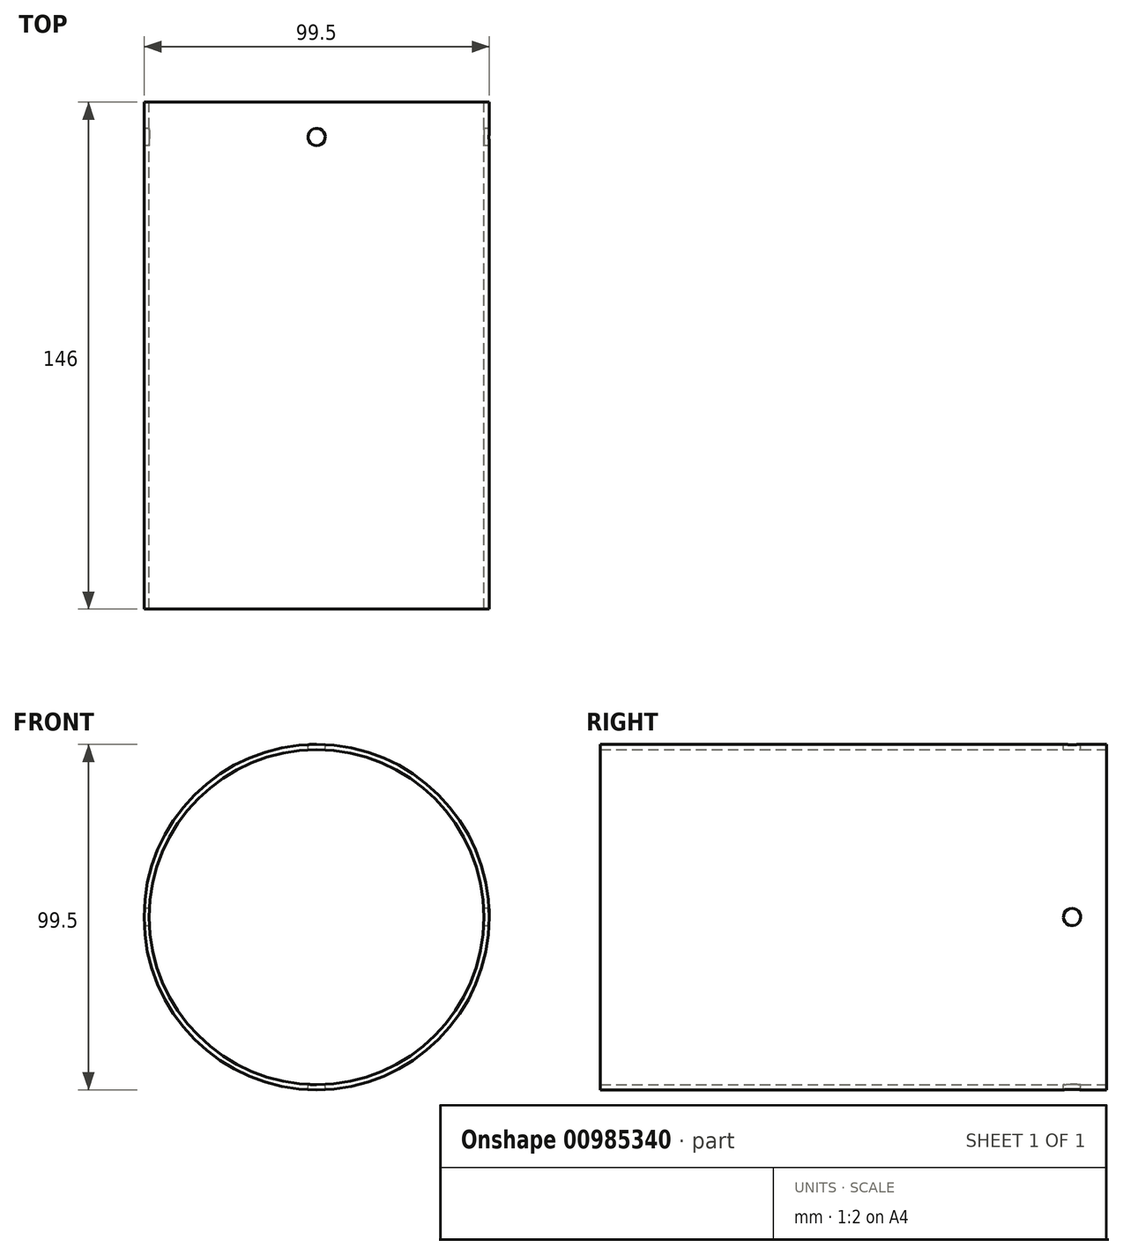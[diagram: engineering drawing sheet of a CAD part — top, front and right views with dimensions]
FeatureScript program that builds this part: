
annotation { "Feature Type Name" : "Feature", "Feature Type Description" : "" }
export const myFeature = defineFeature(function(context is Context, id is Id, definition is map)
    precondition{}
    {
        {
            var Q0;
            Q0=qCreatedBy(makeId("Front.planeOp"),FACE);
            var sketch = newSketch(context, id + "F0", { "sketchPlane" : qUnion([Q0])});
            skCircle(sketch, "E0", {"center": v(0, 0) * mm, "radius": 48.25 * mm});
            skCircle(sketch, "E1", {"center": v(0, 0) * mm, "radius": 49.75 * mm});
            skSolve(sketch);
        }
        {
            var Q0;
            Q0=makeQuery(id+"F0.imprint","IMPRINT",FACE,{"disambiguationData":[TD([[makeQuery(id+"F0.imprint","IMPRINT",EDGE,{"derivedFrom":sQuery(id+"F0.wireOp",EDGE,"E0")}),-1.0]])]});
            extrude(context, id + "F1", {"entities" : qUnion([Q0]), "endBound" : BoundingType.SYMMETRIC, "depth" : 146 * mm});
        }
        {
            var Q0;
            Q0=qCreatedBy(makeId("Top.planeOp"),FACE);
            var sketch = newSketch(context, id + "F2", { "sketchPlane" : qUnion([Q0])});
            skCircle(sketch, "E2", {"center": v(0, 63) * mm, "radius": 2.5 * mm});
            skSolve(sketch);
        }
        {
            var Q0;
            Q0=qCreatedBy(makeId("Right.planeOp"),FACE);
            var sketch = newSketch(context, id + "F3", { "sketchPlane" : qUnion([Q0])});
            skCircle(sketch, "E3", {"center": v(63, 0) * mm, "radius": 2.5 * mm});
            skSolve(sketch);
        }
        {
            var Q0;
            Q0=makeQuery(id+"F3.imprint","IMPRINT",FACE,{"disambiguationData":[TD([[makeQuery(id+"F3.imprint","IMPRINT",EDGE,{"derivedFrom":sQuery(id+"F3.wireOp",EDGE,"E3")}),1.0]])]});
            extrude(context, id + "F4", {"entities" : qUnion([Q0]), "operationType" : NewBodyOperationType.REMOVE, "endBound" : BoundingType.THROUGH_ALL, "depth" : 25 * mm, "hasSecondDirection" : true, "secondDirectionBound" : SecondDirectionBoundingType.THROUGH_ALL, "secondDirectionOppositeDirection" : true, "secondDirectionDepth" : 25 * mm});
        }
        {
            var Q0;
            Q0=makeQuery(id+"F2.imprint","IMPRINT",FACE,{"disambiguationData":[TD([[makeQuery(id+"F2.imprint","IMPRINT",EDGE,{"derivedFrom":sQuery(id+"F2.wireOp",EDGE,"E2")}),1.0]])]});
            extrude(context, id + "F5", {"entities" : qUnion([Q0]), "operationType" : NewBodyOperationType.REMOVE, "endBound" : BoundingType.THROUGH_ALL, "oppositeDirection" : true, "depth" : 25 * mm, "hasSecondDirection" : true, "secondDirectionBound" : SecondDirectionBoundingType.THROUGH_ALL, "secondDirectionOppositeDirection" : false, "secondDirectionDepth" : 25 * mm});
        }
    });
